FCSTD DOCUMENT  (FreeCAD 1.0R39319 (Git))
Label: dxf
License: All rights reserved
LicenseURL: https://en.wikipedia.org/wiki/All_rights_reserved
objects: Sketcher::SketchObject×1, PartDesign::Body×1
note: 3 computed .brp shape members not serialized (recipe doc carries the construction recipe); baked Part::Feature solids carry a one-line shape summary decoded from their .brp

FEATURE [Sketcher::SketchObject] Sketch
  ArcFitTolerance = 1e-06
  AttachmentSupport = -> [XY_Plane]
  FullyConstrained = true
  MakeInternals = false
  MapMode = 5
  sketch-geometry (25):
    g0: LineSegment StartX=-100 StartY=161.716 StartZ=0 EndX=-100 EndY=-161.716 EndZ=0
    g1: LineSegment StartX=-71.7164 StartY=-190 StartZ=0 EndX=71.7164 EndY=-190 EndZ=0
    g2: LineSegment StartX=100 StartY=-161.716 StartZ=0 EndX=100 EndY=161.716 EndZ=0
    g3: LineSegment StartX=71.7164 StartY=190 StartZ=0 EndX=-71.7164 EndY=190 EndZ=0
    g4: ArcOfCircle CenterX=-90 CenterY=160.472 CenterZ=0 NormalX=0 NormalY=0 NormalZ=1 AngleXU=0 Radius=4.25 StartAngle=1.5708 EndAngle=4.71239
    g5: ArcOfCircle CenterX=90 CenterY=160.472 CenterZ=0 NormalX=0 NormalY=0 NormalZ=1 AngleXU=0 Radius=4.25 StartAngle=4.71239 EndAngle=7.85398
    g6: LineSegment StartX=-90 StartY=164.722 StartZ=0 EndX=90 EndY=164.722 EndZ=0
    g7: LineSegment StartX=-90 StartY=156.222 StartZ=0 EndX=90 EndY=156.222 EndZ=0
    g8: Circle CenterX=-90 CenterY=124.74 CenterZ=0 NormalX=0 NormalY=0 NormalZ=1 AngleXU=0 Radius=4
    g9: Circle CenterX=-90 CenterY=90.7559 CenterZ=0 NormalX=0 NormalY=0 NormalZ=1 AngleXU=0 Radius=4
    g10: Circle CenterX=-90 CenterY=56.7713 CenterZ=0 NormalX=0 NormalY=0 NormalZ=1 AngleXU=0 Radius=4
    g11: Circle CenterX=90 CenterY=124.74 CenterZ=0 NormalX=0 NormalY=0 NormalZ=1 AngleXU=0 Radius=4
    g12: Circle CenterX=90 CenterY=90.7559 CenterZ=0 NormalX=0 NormalY=0 NormalZ=1 AngleXU=0 Radius=4
    g13: Circle CenterX=90 CenterY=56.7713 CenterZ=0 NormalX=0 NormalY=0 NormalZ=1 AngleXU=0 Radius=4
    g14: LineSegment [constr] StartX=90 StartY=124.74 StartZ=0 EndX=90 EndY=90.7559 EndZ=0
    g15: LineSegment [constr] StartX=90 StartY=90.7559 StartZ=0 EndX=90 EndY=56.7713 EndZ=0
    g16: Circle CenterX=0 CenterY=-140.655 CenterZ=0 NormalX=0 NormalY=0 NormalZ=1 AngleXU=0 Radius=4
    g17: ArcOfCircle CenterX=-71.7164 CenterY=161.716 CenterZ=0 NormalX=0 NormalY=0 NormalZ=1 AngleXU=0 Radius=28.2836 StartAngle=1.5708 EndAngle=3.14159
    g18: GeomPoint [constr] X=-100 Y=190 Z=0
    g19: ArcOfCircle CenterX=71.7164 CenterY=161.716 CenterZ=0 NormalX=0 NormalY=0 NormalZ=1 AngleXU=0 Radius=28.2836 StartAngle=4e-16 EndAngle=1.5708
    g20: GeomPoint [constr] X=100 Y=190 Z=0
    g21: ArcOfCircle CenterX=71.7164 CenterY=-161.716 CenterZ=0 NormalX=0 NormalY=0 NormalZ=1 AngleXU=0 Radius=28.2836 StartAngle=4.71239 EndAngle=6.28319
    g22: GeomPoint [constr] X=100 Y=-190 Z=0
    g23: ArcOfCircle CenterX=-71.7164 CenterY=-161.716 CenterZ=0 NormalX=0 NormalY=0 NormalZ=1 AngleXU=0 Radius=28.2836 StartAngle=3.14159 EndAngle=4.71239
    g24: GeomPoint [constr] X=-100 Y=-190 Z=0
  constraints (61):
    c: Vertical(g0)
    c: Vertical(g2)
    c: Horizontal(g1)
    c: Horizontal(g3)
    c: Symmetric(g18,g22,g-1)
    c: DistanceX(g18,g20) = 200
    c: DistanceY(g24,g18) = 380
    c: Tangent(g4,g6) = 1.5708
    c: Tangent(g4,g7) = -1.5708
    c: Tangent(g5,g6) = 1.5708
    c: Tangent(g5,g7) = -1.5708
    c: Equal(g4,g5)
    c: Symmetric(g5,g4,g-2)
    c: DistanceX(g6,g6) = 180
    c: Radius(g5) = 4.25
    c: Vertical(g13,g12)
    c: Vertical(g12,g11)
    c: Vertical(g11,g5)
    c: Equal(g11,g12)
    c: Equal(g12,g13)
    c: Equal(g13,g8)
    c: Equal(g8,g9)
    c: Equal(g9,g10)
    c: Vertical(g10,g9)
    c: Vertical(g9,g8)
    c: Vertical(g8,g4)
    c: Horizontal(g8,g11)
    c: Horizontal(g9,g12)
    c: Horizontal(g10,g13)
    c: Diameter(g11) = 8
    c: Coincident(g14,g11)
    c: Coincident(g14,g12)
    c: Coincident(g14,g15)
    c: Coincident(g15,g13)
    c: Equal(g15,g14)
    c: DistanceY(g14,g14) = 33.9846
    c: Distance(g5,g3) = 29.5283
    c: DistanceY(g11,g5) = 35.7312
    c: PointOnObject(g16,g-2)
    c: Equal(g16,g11)
    c: Distance(g16,g1) = 49.3454
    c: PointOnObject(g18,g0)
    c: PointOnObject(g18,g3)
    c: Tangent(g0,g17) = -1.5708
    c: Tangent(g3,g17) = -1.5708
    c: PointOnObject(g20,g2)
    c: PointOnObject(g20,g3)
    c: Tangent(g2,g19) = -1.5708
    c: Tangent(g3,g19) = -1.5708
    c: PointOnObject(g22,g1)
    c: PointOnObject(g22,g2)
    c: Tangent(g1,g21) = -1.5708
    c: Tangent(g2,g21) = -1.5708
    c: PointOnObject(g24,g0)
    c: PointOnObject(g24,g1)
    c: Tangent(g0,g23) = -1.5708
    c: Tangent(g1,g23) = -1.5708
    c: Equal(g21,g23)
    c: Equal(g23,g17)
    c: Equal(g17,g19)
    c: Radius(g21) = 28.2836
FEATURE [PartDesign::Body] Body
  AllowCompound = false
  Group = -> [Sketch]
  Origin = -> Origin
